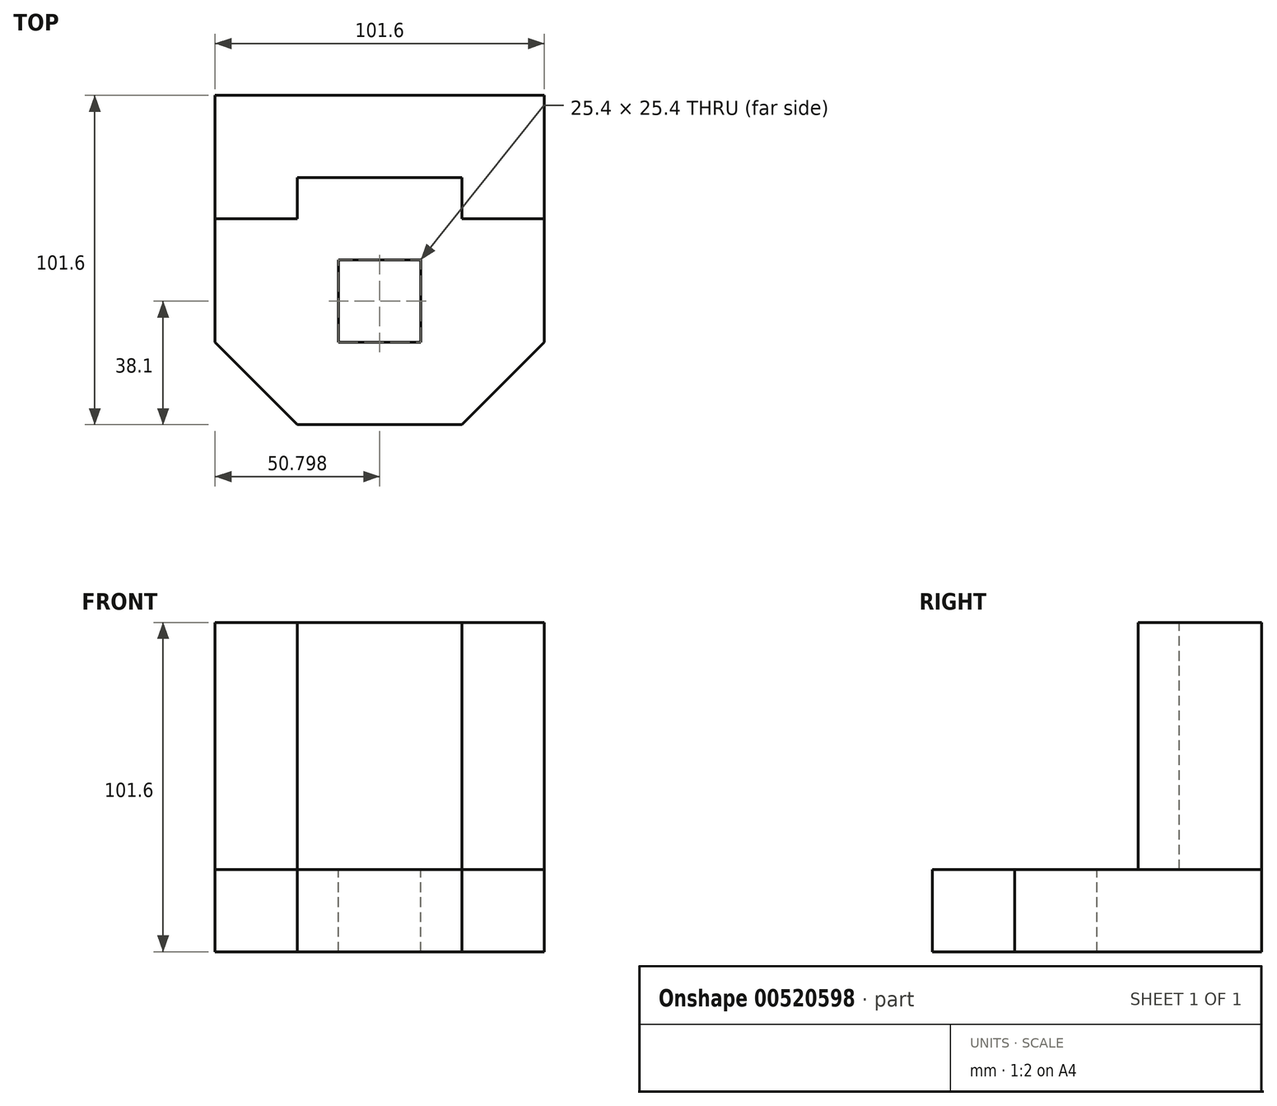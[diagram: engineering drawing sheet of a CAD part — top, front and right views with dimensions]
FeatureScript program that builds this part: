
annotation { "Feature Type Name" : "Feature", "Feature Type Description" : "" }
export const myFeature = defineFeature(function(context is Context, id is Id, definition is map)
    precondition{}
    {
        {
            var Q0;
            Q0=qCreatedBy(makeId("Top.planeOp"),FACE);
            var sketch = newSketch(context, id + "F0", { "sketchPlane" : qUnion([Q0])});
            skLineSegment(sketch, "E0", {"start": v(0, 50.8) * mm, "end": v(-50.8, 50.8) * mm});
            skLineSegment(sketch, "E1", {"start": v(-50.8, 50.8) * mm, "end": v(-50.8, -25.4) * mm});
            skLineSegment(sketch, "E2", {"start": v(0, 50.8) * mm, "end": v(50.8, 50.8) * mm});
            skLineSegment(sketch, "E3", {"start": v(50.8, 50.8) * mm, "end": v(50.8, -25.4) * mm});
            skLineSegment(sketch, "E4", {"start": v(0, -50.8) * mm, "end": v(-25.4, -50.8) * mm});
            skLineSegment(sketch, "E5", {"start": v(0, -50.8) * mm, "end": v(25.4, -50.8) * mm});
            skLineSegment(sketch, "E6", {"start": v(-50.8, -25.4) * mm, "end": v(-25.4, -50.8) * mm});
            skLineSegment(sketch, "E7", {"start": v(50.8, -25.4) * mm, "end": v(25.4, -50.8) * mm});
            skSolve(sketch);
        }
        {
            var Q0;
            Q0=makeQuery(id+"F0.imprint","IMPRINT",FACE,{"disambiguationData":[TD([[makeQuery(id+"F0.imprint","IMPRINT",EDGE,{"derivedFrom":sQuery(id+"F0.wireOp",EDGE,"E0")}),1.0]])]});
            extrude(context, id + "F1", {"entities" : qUnion([Q0]), "oppositeDirection" : true, "depth" : 50.8 * mm, "offsetDistance" : 25.4 * mm});
        }
        {
            var Q0;
            Q0=makeQuery(id+"F1.opExtrude","CAP_FACE",FACE,{"disambiguationData":[OSD([sQuery(id+"F0.wireOp",EDGE,"E0"),sQuery(id+"F0.wireOp",EDGE,"E1"),sQuery(id+"F0.wireOp",EDGE,"E2"),sQuery(id+"F0.wireOp",EDGE,"E3"),sQuery(id+"F0.wireOp",EDGE,"E4"),sQuery(id+"F0.wireOp",EDGE,"E5"),sQuery(id+"F0.wireOp",EDGE,"E6"),sQuery(id+"F0.wireOp",EDGE,"E7")])],"isStart":true});
            extrude(context, id + "F2", {"entities" : qUnion([Q0]), "operationType" : NewBodyOperationType.REMOVE, "oppositeDirection" : true, "depth" : 25.4 * mm, "offsetDistance" : 25.4 * mm});
        }
        {
            var Q0;
            Q0=qCreatedBy(makeId("Top.planeOp"),FACE);
            var sketch = newSketch(context, id + "F3", { "sketchPlane" : qUnion([Q0])});
            skLineSegment(sketch, "E8", {"start": v(12.7, -25.4) * mm, "end": v(12.7, 0) * mm});
            skLineSegment(sketch, "E9", {"start": v(12.7, 0) * mm, "end": v(-12.7, 0) * mm});
            skLineSegment(sketch, "E10", {"start": v(12.7, -25.4) * mm, "end": v(-12.7, -25.4) * mm});
            skLineSegment(sketch, "E11", {"start": v(-12.7, -25.4) * mm, "end": v(-12.7, 0) * mm});
            skLineSegment(sketch, "E12", {"start": v(-12.7, 0) * mm, "end": v(12.7, 0) * mm});
            skSolve(sketch);
        }
        {
            var Q0;
            Q0 = qSketchRegion(id + "F3", true);
            extrude(context, id + "F4", {"entities" : qUnion([Q0]), "operationType" : NewBodyOperationType.ADD, "oppositeDirection" : true, "depth" : 50.8 * mm, "offsetDistance" : 25.4 * mm});
        }
        {
            var Q0;
            Q0=makeQuery(id+"F4.opExtrude","CAP_FACE",FACE,{"disambiguationData":[OSD([sQuery(id+"F3.wireOp",EDGE,"E8"),sQuery(id+"F3.wireOp",EDGE,"E10"),sQuery(id+"F3.wireOp",EDGE,"E11"),sQuery(id+"F3.wireOp",EDGE,"E12")])],"isStart":true});
            extrude(context, id + "F5", {"entities" : qUnion([Q0]), "operationType" : NewBodyOperationType.REMOVE, "oppositeDirection" : true, "depth" : 67.06 * mm, "offsetDistance" : 25.4 * mm});
        }
        {
            var Q0;
            Q0=qCreatedBy(makeId("Top.planeOp"),FACE);
            var sketch = newSketch(context, id + "F6", { "sketchPlane" : qUnion([Q0])});
            skLineSegment(sketch, "E13", {"start": v(0, 50.8) * mm, "end": v(-50.8, 50.8) * mm});
            skLineSegment(sketch, "E14", {"start": v(-50.8, 50.8) * mm, "end": v(-50.8, 12.7) * mm});
            skLineSegment(sketch, "E15", {"start": v(-50.8, 12.7) * mm, "end": v(-25.4, 12.7) * mm});
            skLineSegment(sketch, "E16", {"start": v(-25.4, 12.7) * mm, "end": v(-25.4, 25.4) * mm});
            skLineSegment(sketch, "E17", {"start": v(0, 50.8) * mm, "end": v(50.8, 50.8) * mm});
            skLineSegment(sketch, "E18", {"start": v(50.8, 50.8) * mm, "end": v(50.8, 12.7) * mm});
            skLineSegment(sketch, "E19", {"start": v(50.8, 12.7) * mm, "end": v(25.4, 12.7) * mm});
            skLineSegment(sketch, "E20", {"start": v(25.4, 12.7) * mm, "end": v(25.4, 25.4) * mm});
            skLineSegment(sketch, "E21", {"start": v(25.4, 25.4) * mm, "end": v(-25.4, 25.4) * mm});
            skSolve(sketch);
        }
        {
            var Q0;
            Q0=makeQuery(id+"F6.imprint","IMPRINT",FACE,{"disambiguationData":[TD([[makeQuery(id+"F6.imprint","IMPRINT",EDGE,{"derivedFrom":sQuery(id+"F6.wireOp",EDGE,"E13")}),1.0]])]});
            extrude(context, id + "F7", {"entities" : qUnion([Q0]), "oppositeDirection" : true, "depth" : 25.4 * mm, "offsetDistance" : 25.4 * mm});
        }
        {
            var Q0;
            Q0=makeQuery(id+"F7.opExtrude","CAP_FACE",FACE,{"disambiguationData":[OSD([sQuery(id+"F6.wireOp",EDGE,"E13"),sQuery(id+"F6.wireOp",EDGE,"E14"),sQuery(id+"F6.wireOp",EDGE,"E15"),sQuery(id+"F6.wireOp",EDGE,"E16"),sQuery(id+"F6.wireOp",EDGE,"E17"),sQuery(id+"F6.wireOp",EDGE,"E18"),sQuery(id+"F6.wireOp",EDGE,"E19"),sQuery(id+"F6.wireOp",EDGE,"E20"),sQuery(id+"F6.wireOp",EDGE,"E21")])],"isStart":true});
            extrude(context, id + "F8", {"entities" : qUnion([Q0]), "operationType" : NewBodyOperationType.ADD, "depth" : 50.8 * mm, "offsetDistance" : 25.4 * mm});
        }
    });
